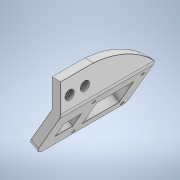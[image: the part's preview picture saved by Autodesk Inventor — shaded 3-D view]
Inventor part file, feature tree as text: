
AUTODESK INVENTOR PART (.ipt)
format: ipt  version: 2021 (Build 250183000, 183)  size: 336,384 bytes
history: native  units: mm
features: extrude x8, sketch x6, projected_geometry x6, thicken_offset x2, revolve x1, fillet x1
ambient origin geometry x8: Origin, YZ Plane, XZ Plane, XY Plane, X Axis, Y Axis, Z Axis, Center Point
bodies: Solid1 (feature_tree)
feature tree (24):
  extrude  "Extrusion1"  Depth=30.23mm
  revolve  "Revolution1"  Angle=30.0deg
  extrude  "Extrusion2"  Depth=60.0mm TaperAngle=0.0deg
  extrude  "Extrusion3"  Depth=4.3mm
  extrude  "Extrusion4"  Depth=8.05mm
  extrude  "Extrusion5"  TaperAngle=0.0deg  [1 undecoded]
  thicken_offset  "Thicken4"
  thicken_offset  "Thicken5"
  extrude  "Extrusion6"  Depth=0.2mm
  extrude  "Extrusion7"  Depth=0.2mm
  extrude  "Extrusion8"  Depth=0.2mm
  fillet  "Fillet3"  Radius=3.2mm
  sketch  "Sketch1"  dims[d0=26.0mm d1=30.23mm]
  sketch  "Sketch2"  dims[d2=8.0mm d3=0.0mm d4=30.0deg]
  projected_geometry  "Projected Loop1"
  sketch  "Sketch3"  dims[d5=50.0mm d6=0.0mm d7=60.0mm d8=0.0mm]
  projected_geometry  "Projected Loop2"
  sketch  "Sketch4"  dims[d9=4.3mm d10=4.3mm]
  projected_geometry  "Projected Loop3"
  projected_geometry  "Projected Loop4"
  sketch  "Sketch7"  dims[d12=11.6mm d13=8.05mm]
  projected_geometry  "Projected Loop5"
  sketch  "Sketch8"  dims[d14=11.6mm d15=0.0mm d16=0.0mm d17=3.2mm d18=3.2mm d19=3.2mm d20=3.2mm d21=48.0mm d22=48.0mm d23=41.0mm d24=41.0mm d29=4.6mm d30=6.6mm d31=33.8mm d32=26.8mm d33=5.5mm d34=5.5mm d35=0.0mm d36=0.0mm d38=10.6mm d39=10.6mm d42=16.0mm d43=16.0mm d48=1.0mm d49=1.0mm d50=4.0mm d51=4.0mm d52=0.0mm d53=0.0mm d55=8.5mm d56=8.5mm d57=4.0mm d58=0.0mm d59=30.23mm d60=4.0mm d61=0.0mm d62=10.0mm d63=10.0mm d64=90.0mm d66=0.2mm]
  projected_geometry  "Projected Loop6"
note: 1 required parameter value undecoded (feature->parameter linkage not recoverable at this tier; creation-order binding heuristic only, values carry confidence <= 0.55)
